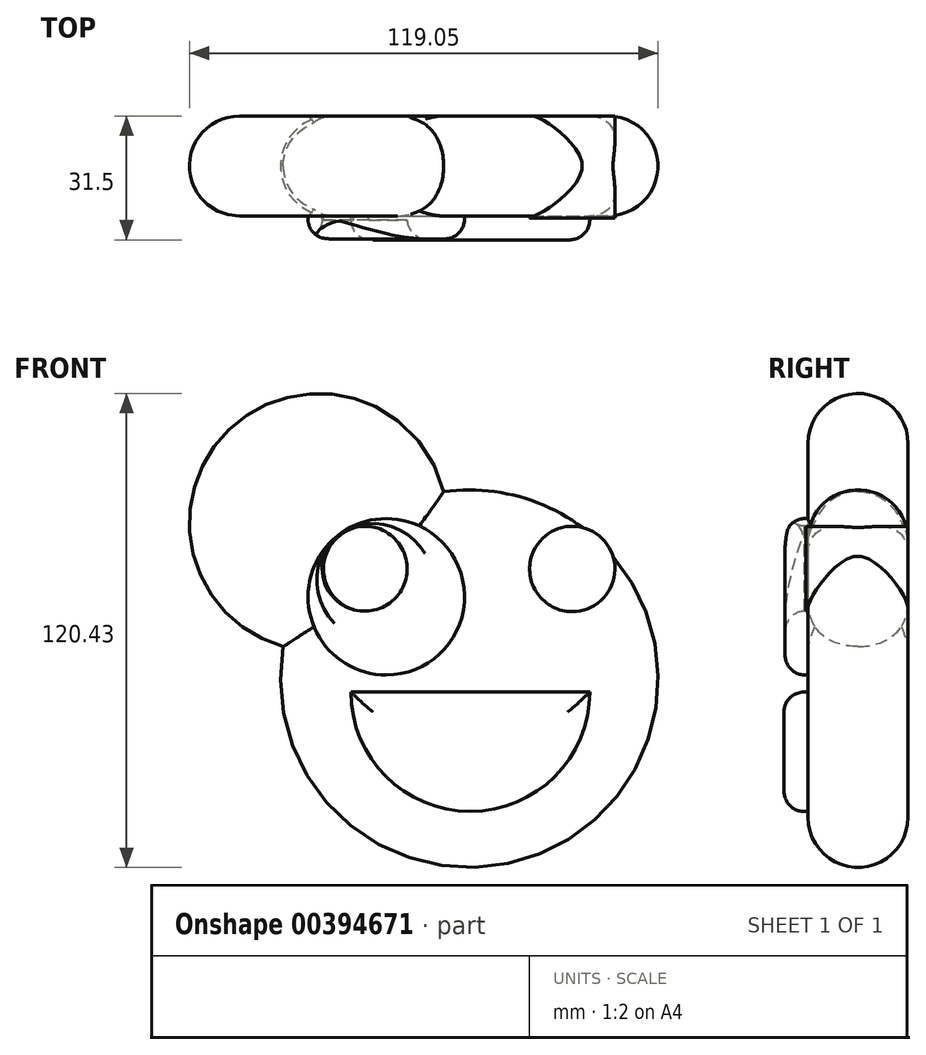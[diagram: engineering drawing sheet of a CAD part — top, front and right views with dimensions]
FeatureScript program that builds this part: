
annotation { "Feature Type Name" : "Feature", "Feature Type Description" : "" }
export const myFeature = defineFeature(function(context is Context, id is Id, definition is map)
    precondition{}
    {
        {
            var Q0;
            Q0=qCreatedBy(makeId("Front.planeOp"),FACE);
            var sketch = newSketch(context, id + "F0", { "sketchPlane" : qUnion([Q0])});
            skCircle(sketch, "E0", {"center": v(0, 0) * mm, "radius": 47.97 * mm});
            skArc(sketch, "E1", {"start": v(-6.49, 47.53) * mm, "mid": v(-61.07, 63.26) * mm, "end": v(-47.27, 8.16) * mm});
            skArc(sketch, "E2.MirrorCS", {"start": v(6.49, 47.53) * mm, "mid": v(61.07, 63.26) * mm, "end": v(47.27, 8.16) * mm});
            skSolve(sketch);
        }
        {
            var Q0;
            {var subQ0=sQuery(id+"F0.wireOp",EDGE,"qMnfbMMB-3m1s-uUW1-9r4w-OCcZsqSqAnbS");var subQ1=sQuery(id+"F0.wireOp",EDGE,"E0");var subQ2=makeQuery(id+"F0.imprint","INTERSECT",VERTEX,{"disambiguationData":[OD(0.0)],"derivedFrom":[subQ1,subQ0]});Q0=makeQuery(id+"F0.imprint","IMPRINT",FACE,{"disambiguationData":[TD([[makeQuery(id+"F0.imprint","IMPRINT",EDGE,{"disambiguationData":[TD([[subQ2,1.0]])],"derivedFrom":subQ1}),-1.0]])]});}
            var Q1;
            {var subQ0=sQuery(id+"F0.wireOp",EDGE,"qMnfbMMB-3m1s-uUW1-9r4w-OCcZsqSqAnbS");var subQ1=sQuery(id+"F0.wireOp",EDGE,"E0");var subQ2=makeQuery(id+"F0.imprint","INTERSECT",VERTEX,{"disambiguationData":[OD(0.0)],"derivedFrom":[subQ1,subQ0]});Q1=makeQuery(id+"F0.imprint","IMPRINT",FACE,{"disambiguationData":[TD([[makeQuery(id+"F0.imprint","IMPRINT",EDGE,{"disambiguationData":[TD([[subQ2,1.0]])],"derivedFrom":subQ1}),1.0]])]});}
            var Q2;
            {var subQ0=sQuery(id+"F0.wireOp",EDGE,"E1");var subQ1=sQuery(id+"F0.wireOp",EDGE,"E0");var subQ2=makeQuery(id+"F0.imprint","INTERSECT",VERTEX,{"disambiguationData":[OD(0.0)],"derivedFrom":[subQ1,subQ0]});Q2=makeQuery(id+"F0.imprint","IMPRINT",FACE,{"disambiguationData":[TD([[makeQuery(id+"F0.imprint","IMPRINT",EDGE,{"disambiguationData":[TD([[subQ2,-1.0]])],"derivedFrom":subQ1}),1.0]])]});}
            var Q3;
            {var subQ0=sQuery(id+"F0.wireOp",EDGE,"E1");var subQ1=sQuery(id+"F0.wireOp",EDGE,"E0");var subQ2=makeQuery(id+"F0.imprint","INTERSECT",VERTEX,{"disambiguationData":[OD(0.0)],"derivedFrom":[subQ1,subQ0]});Q3=makeQuery(id+"F0.imprint","IMPRINT",FACE,{"disambiguationData":[TD([[makeQuery(id+"F0.imprint","IMPRINT",EDGE,{"disambiguationData":[TD([[subQ2,-1.0]])],"derivedFrom":subQ1}),-1.0]])]});}
            var Q4;
            {var subQ0=sQuery(id+"F0.wireOp",EDGE,"E2.MirrorCS");Q4=makeQuery(id+"F0.imprint","IMPRINT",FACE,{"disambiguationData":[TD([[makeQuery(id+"F0.imprint","IMPRINT",EDGE,{"derivedFrom":subQ0}),-1.0]])]});}
            extrude(context, id + "F1", {"entities" : qUnion([Q0, Q1, Q2, Q3, Q4]), "depth" : 25.4 * mm});
        }
        {
            var Q0;
            Q0=makeQuery(id+"F1.opExtrude","CAP_FACE",FACE,{"disambiguationData":[OSD([sQuery(id+"F0.wireOp",EDGE,"E0"),sQuery(id+"F0.wireOp",EDGE,"E1"),sQuery(id+"F0.wireOp",EDGE,"E2.MirrorCS")])],"isStart":false});
            fillet(context, id + "F2", {"entities" : qUnion([Q0]), "radius" : 12.7 * mm, "tangentPropagation" : true, "allowEdgeOverflow" : false});
        }
        {
            var Q0;
            Q0=makeQuery(id+"F1.opExtrude","CAP_FACE",FACE,{"disambiguationData":[OSD([sQuery(id+"F0.wireOp",EDGE,"E0"),sQuery(id+"F0.wireOp",EDGE,"E1"),sQuery(id+"F0.wireOp",EDGE,"E2.MirrorCS")])],"isStart":true});
            fillet(context, id + "F3", {"entities" : qUnion([Q0]), "radius" : 12.7 * mm, "tangentPropagation" : true, "allowEdgeOverflow" : false});
        }
        {
            var Q0;
            Q0=qCreatedBy(makeId("Front.planeOp"),FACE);
            var sketch = newSketch(context, id + "F4", { "sketchPlane" : qUnion([Q0])});
            skCircle(sketch, "E3", {"center": v(-21.08, 20.8) * mm, "radius": 19.87 * mm});
            skCircle(sketch, "E4.MirrorC", {"center": v(21.08, 20.8) * mm, "radius": 19.87 * mm});
            skCircle(sketch, "E5", {"center": v(-26.58, 27.95) * mm, "radius": 10.8 * mm});
            skCircle(sketch, "E6.MirrorC", {"center": v(26.58, 27.95) * mm, "radius": 10.8 * mm});
            skSolve(sketch);
        }
        {
            var Q0;
            Q0=makeQuery(id+"F4.imprint","IMPRINT",FACE,{"disambiguationData":[TD([[makeQuery(id+"F4.imprint","IMPRINT",EDGE,{"derivedFrom":sQuery(id+"F4.wireOp",EDGE,"E4.MirrorC")}),-1.0]])]});
            var Q1;
            Q1=makeQuery(id+"F4.imprint","IMPRINT",FACE,{"disambiguationData":[TD([[makeQuery(id+"F4.imprint","IMPRINT",EDGE,{"derivedFrom":sQuery(id+"F4.wireOp",EDGE,"E3")}),1.0]])]});
            extrude(context, id + "F5", {"entities" : qUnion([Q0, Q1]), "operationType" : NewBodyOperationType.ADD, "depth" : 31.24 * mm});
        }
        {
            var Q0;
            Q0=makeQuery(id+"F5.opExtrude","CAP_FACE",FACE,{"disambiguationData":[OSD([sQuery(id+"F4.wireOp",EDGE,"E4.MirrorC"),sQuery(id+"F4.wireOp",EDGE,"E6.MirrorC")])],"isStart":false});
            var Q1;
            Q1=makeQuery(id+"F5.opExtrude","CAP_FACE",FACE,{"disambiguationData":[OSD([sQuery(id+"F4.wireOp",EDGE,"E3"),sQuery(id+"F4.wireOp",EDGE,"E5")])],"isStart":false});
            fillet(context, id + "F6", {"entities" : qUnion([Q0, Q1]), "radius" : 5.08 * mm, "tangentPropagation" : true, "allowEdgeOverflow" : false});
        }
        {
            var Q0;
            Q0=qCreatedBy(makeId("Front.planeOp"),FACE);
            var sketch = newSketch(context, id + "F7", { "sketchPlane" : qUnion([Q0])});
            skCircle(sketch, "E7", {"center": v(-26.18, 27.88) * mm, "radius": 10.84 * mm});
            skPoint(sketch, "E7.first.point", {"position": v(-33.54, 35.83) * mm});
            skPoint(sketch, "E7.second.point", {"position": v(-19.06, 19.7) * mm});
            skPoint(sketch, "E7.third.point", {"position": v(-15.58, 30.15) * mm});
            skCircle(sketch, "E8.MirrorC", {"center": v(26.18, 27.88) * mm, "radius": 10.84 * mm});
            skSolve(sketch);
        }
        {
            var Q0;
            Q0=makeQuery(id+"F7.imprint","IMPRINT",FACE,{"disambiguationData":[TD([[makeQuery(id+"F7.imprint","IMPRINT",EDGE,{"derivedFrom":sQuery(id+"F7.wireOp",EDGE,"E7")}),1.0]])]});
            extrude(context, id + "F8", {"entities" : qUnion([Q0]), "operationType" : NewBodyOperationType.ADD, "depth" : 26.42 * mm});
        }
        {
            var Q0;
            Q0 = qSketchRegion(id + "F7", true);
            extrude(context, id + "F9", {"entities" : qUnion([Q0]), "operationType" : NewBodyOperationType.ADD, "depth" : 25.9 * mm});
        }
        {
            var Q0;
            {var subQ0=sQuery(id+"F0.wireOp",EDGE,"E1");var subQ1=sQuery(id+"F0.wireOp",EDGE,"E0");var subQ2=sQuery(id+"F0.wireOp",EDGE,"E2.MirrorCS");Q0=makeQuery(id+"F5.boolean.opBoolean","SPLIT",FACE,{"disambiguationData":[TD([makeQuery(id+"F2.opFillet","BLEND_FACE",FACE,{"disambiguationData":[OSD([subQ1]),TDD([makeQuery(id+"F1.opExtrude","CAP_EDGE",EDGE,{"disambiguationData":[OSD([subQ1]),TDD([makeQuery(id+"F0.imprint","IMPRINT",EDGE,{"disambiguationData":[TD([[makeQuery(id+"F0.imprint","INTERSECT",VERTEX,{"disambiguationData":[OD(0.0)],"derivedFrom":[subQ1,subQ0]}),1.0]])],"derivedFrom":subQ1})])],"isStart":false})])]}),makeQuery(id+"F2.opFillet","BLEND_FACE",FACE,{"disambiguationData":[OSD([subQ1]),TDD([makeQuery(id+"F1.opExtrude","CAP_EDGE",EDGE,{"disambiguationData":[OSD([subQ1]),TDD([makeQuery(id+"F0.imprint","IMPRINT",EDGE,{"disambiguationData":[TD([[makeQuery(id+"F0.imprint","INTERSECT",VERTEX,{"disambiguationData":[OD(1.0)],"derivedFrom":[subQ1,subQ0]}),-1.0]])],"derivedFrom":subQ1})])],"isStart":false})])]}),makeQuery(id+"F5.opExtrude","SWEPT_FACE",FACE,{"disambiguationData":[OSD([sQuery(id+"F4.wireOp",EDGE,"E3")])]}),makeQuery(id+"F5.opExtrude","SWEPT_FACE",FACE,{"disambiguationData":[OSD([sQuery(id+"F4.wireOp",EDGE,"E4.MirrorC")])]})])],"derivedFrom":makeQuery(id+"F1.opExtrude","CAP_FACE",FACE,{"disambiguationData":[OSD([subQ1,subQ0,subQ2])],"isStart":false})});}
            var sketch = newSketch(context, id + "F10", { "sketchPlane" : qUnion([Q0])});
            skLineSegment(sketch, "E9", {"start": v(-30.06, -3.4) * mm, "end": v(30.61, -3.4) * mm});
            skArc(sketch, "E10", {"start": v(30.61, -3.4) * mm, "mid": v(0.27, -33.73) * mm, "end": v(-30.06, -3.4) * mm});
            skSolve(sketch);
        }
        {
            var Q0;
            Q0=makeQuery(id+"F10.imprint","IMPRINT",FACE,{"disambiguationData":[TD([[makeQuery(id+"F10.imprint","IMPRINT",EDGE,{"derivedFrom":sQuery(id+"F10.wireOp",EDGE,"E9")}),-1.0]])]});
            extrude(context, id + "F11", {"entities" : qUnion([Q0]), "operationType" : NewBodyOperationType.ADD, "depth" : 6.1 * mm});
        }
        {
            var Q0;
            Q0=makeQuery(id+"F11.opExtrude","CAP_FACE",FACE,{"disambiguationData":[OSD([sQuery(id+"F10.wireOp",EDGE,"E9"),sQuery(id+"F10.wireOp",EDGE,"E10")])],"isStart":false});
            fillet(context, id + "F12", {"entities" : qUnion([Q0]), "radius" : 5.08 * mm, "tangentPropagation" : true, "allowEdgeOverflow" : false});
        }
    });
